# Revit family: Hager-IC-Flush_mounted-IP40-With_Cover-Horiz-With_DIN-Hosted-PL-pl
name_source: partatom
category: Electrical Equipment
units: mm (PartAtom-declared; Revit-internal decimal feet)

## family parameters
Cut with Voids When Loaded = No
Host = Face
Maintain Annotation Orientation = Yes
Panel Configuration = Two Columns, Circuits Across
Part Type = Panelboard
Room Calculation Point = No
Round Connector Dimension = Use Diameter
Shared = No

## types (6) — shared parameters
BC_MODEL_ID = 1591955
BC_OBJECT_ID = 518334
BC_OBJECT_VERSION = #1
Code hager = ADD-EC000214_EUHD
EF000003 - Mounting method = Flush-mounted
EF000007 - Colour = White
EF000024 - UV resistant = No
EF000049 - Depth = 91 mm  [stored 0.298556 ft]
EF000116 - RAL-number = 9010
EF000118 - With mounting plate = No
EF000218 - Built-in depth = 72 mm  [stored 0.23622 ft]
EF000266 - Number of rows = 1
EF000339 - Type of covering = Door
EF001062 - EMC-version = No
EF001088 - Extension possible = Yes
EF001131 - Inner depth = 72 mm  [stored 0.23622 ft]
EF001134 - DIN-rail = Yes
EF001596 - Housing material = Plastic
EF004462 - Type of closure = Other
EF004464 - Type of door = Single
EF005474 - Degree of protection (IP) = IP40
EF006306 - With lock = No
EF009212 - Cover model = Closed
EF015776 - Earthing terminal block = Yes
EF015777 - Neutral terminal block = Yes
EF015941 - Signal passing door = Yes
ETIM class code = EC000214
ETIM class name = Small distribution board
HG000002-With door or cover = Yes
HG000003-Range = IC
HG000005-Thickness = 2 mm  [stored 0.00656168 ft]
HG000006-Flush mounted = Yes
HG000012-Door swing angle = 90.00°
HG000015-Clearance visibility = Yes
HG000016-Door 3D visibility = Yes
HG000017-Distance between poles = 18 mm  [stored 0.0590551 ft]
HG000060-RAL-number = 9010
HG000099-Onfly Template ID = 1539781
HGEF000266-Number of rows = 1
Manufacturer = Hager
Name = IC-Flush_mounted-IP40-With_Cover-Horiz-With_DIN-PL
Name BIM&CO = Electricity
Name hager = ADD_Enclosures_EC000214
Uniformat = Low Tension Service & Dist.
Uniformat code = D501001
zero-valued in all types: Default Elevation

## per-type parameters (varying)
| type | BC_VARIANT_ID | EF000008 - Width | EF000040 - Height | EF000332 - Built-in height | EF000846 - Built-in width | EF002950 - Width in number of modular spacings | EF006244 - Transparent cover/door | HG000004-Manufacturer reference | HGEF002950-Width in number of modular spacings |
| IC-Flush_mounted_W236_H206_D91_8_Modular_Spacing-VR108PP | 1196660 | 236 mm | 206 mm  [stored 0.675853 ft] | 188 mm  [stored 0.616798 ft] | 218 mm  [stored 0.715223 ft] | 8 | No | VR108PP | 8 |
| IC-Flush_mounted_W236_H206_D91_8_Modular_Spacing-VR108TP | 1196661 | 236 mm | 206 mm  [stored 0.675853 ft] | 188 mm  [stored 0.616798 ft] | 218 mm  [stored 0.715223 ft] | 8 | Yes | VR108TP | 8 |
| IC-Flush_mounted_W308_H226_D91_12_Modular_Spacing-VR112PP | 1196662 | 308 mm  [stored 1.0105 ft] | 226 mm  [stored 0.74147 ft] | 208 mm | 290 mm  [stored 0.951444 ft] | 12 | No | VR112PP | 12 |
| IC-Flush_mounted_W308_H226_D91_12_Modular_Spacing-VR112TP | 1196663 | 308 mm  [stored 1.0105 ft] | 226 mm  [stored 0.74147 ft] | 208 mm | 290 mm  [stored 0.951444 ft] | 12 | Yes | VR112TP | 12 |
| IC-Flush_mounted_W416_H226_D91_18_Modular_Spacing-VR118PP | 1196664 | 416 mm | 226 mm  [stored 0.74147 ft] | 208 mm | 398 mm  [stored 1.30577 ft] | 18 | No | VR118PP | 18 |
| IC-Flush_mounted_W416_H226_D91_18_Modular_Spacing-VR118TP | 1196665 | 416 mm | 226 mm  [stored 0.74147 ft] | 208 mm | 398 mm  [stored 1.30577 ft] | 18 | Yes | VR118TP | 18 |

note: column(s) folded — value = type name in every type: Reference, Reference description

note: [stored X ft] marks values corroborated as IEEE doubles in the binary element streams (Revit-internal decimal feet)

## geometry (parser evidence)
native form markers: Sweep x15
no freeform markers — native parametric forms only
